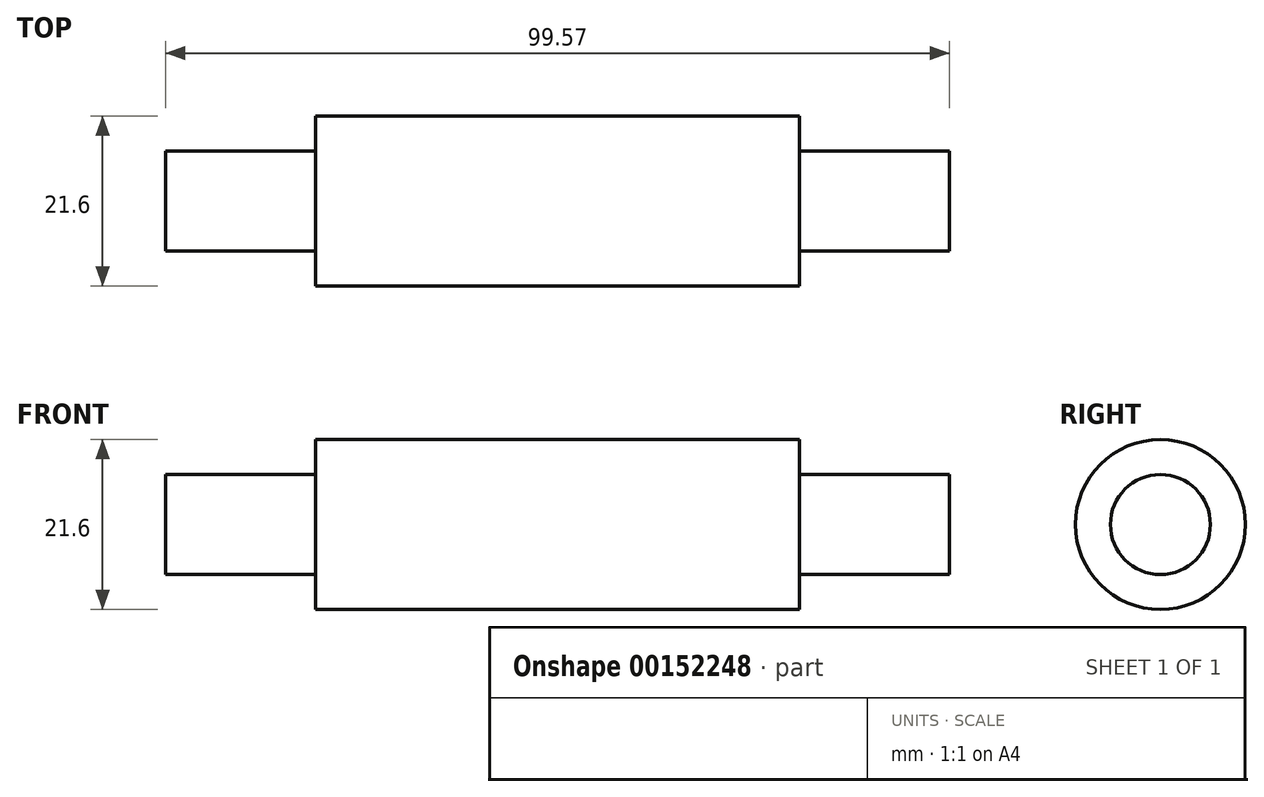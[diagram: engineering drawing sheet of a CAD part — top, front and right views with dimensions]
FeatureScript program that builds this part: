
annotation { "Feature Type Name" : "Feature", "Feature Type Description" : "" }
export const myFeature = defineFeature(function(context is Context, id is Id, definition is map)
    precondition{}
    {
        {
            var Q0;
            Q0=qCreatedBy(makeId("Front.planeOp"),FACE);
            var sketch = newSketch(context, id + "F0", { "sketchPlane" : qUnion([Q0])});
            skLineSegment(sketch, "E0", {"start": v(0, 0) * mm, "end": v(61.47, 0) * mm});
            skLineSegment(sketch, "E1", {"start": v(61.47, 6.35) * mm, "end": v(61.47, 10.8) * mm});
            skLineSegment(sketch, "E2", {"start": v(61.47, 10.8) * mm, "end": v(0, 10.8) * mm});
            skLineSegment(sketch, "E3", {"start": v(0, 10.8) * mm, "end": v(0, 6.35) * mm});
            skLineSegment(sketch, "E4", {"start": v(61.47, 0) * mm, "end": v(80.52, 0) * mm});
            skLineSegment(sketch, "E5", {"start": v(80.52, 0) * mm, "end": v(80.52, 6.35) * mm});
            skLineSegment(sketch, "E6", {"start": v(80.52, 6.35) * mm, "end": v(61.47, 6.35) * mm});
            skLineSegment(sketch, "E7", {"start": v(0, 0) * mm, "end": v(-19.05, 0) * mm});
            skLineSegment(sketch, "E8", {"start": v(-19.05, 0) * mm, "end": v(-19.05, 6.35) * mm});
            skLineSegment(sketch, "E9", {"start": v(-19.05, 6.35) * mm, "end": v(0, 6.35) * mm});
            skSolve(sketch);
        }
        {
            var Q0;
            Q0=makeQuery(id+"F0.imprint","IMPRINT",FACE,{"disambiguationData":[TD([[makeQuery(id+"F0.imprint","IMPRINT",EDGE,{"derivedFrom":sQuery(id+"F0.wireOp",EDGE,"E0")}),1.0]])]});
            var Q1;
            Q1=sQuery(id+"F0.wireOp",EDGE,"E0");
            revolve(context, id + "F1", {"entities" : qUnion([Q0]), "axis" : qUnion([Q1]), "revolveType" : RevolveType.FULL});
        }
    });
